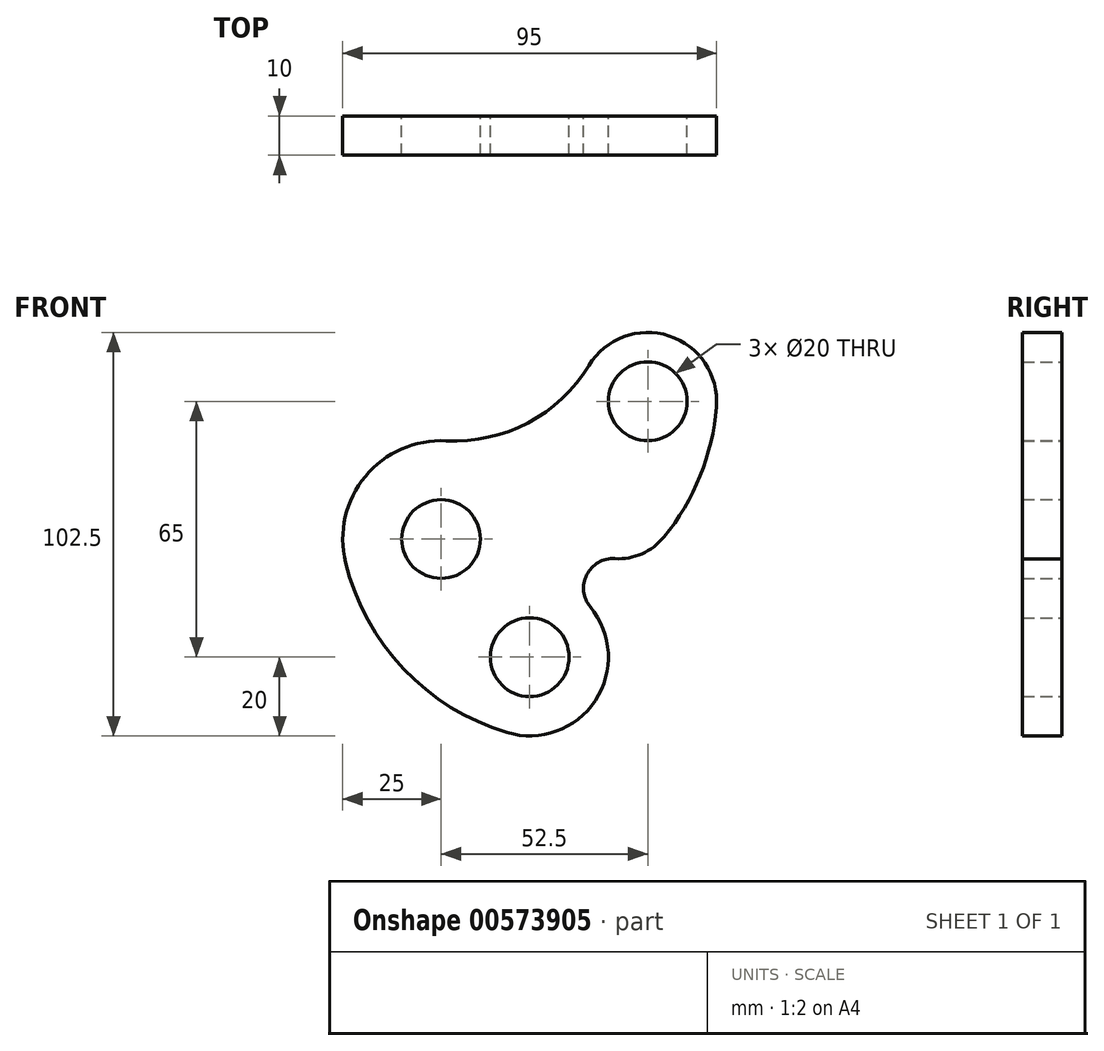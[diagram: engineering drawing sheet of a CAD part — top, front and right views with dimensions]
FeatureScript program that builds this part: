
annotation { "Feature Type Name" : "Feature", "Feature Type Description" : "" }
export const myFeature = defineFeature(function(context is Context, id is Id, definition is map)
    precondition{}
    {
        {
            var Q0;
            Q0=qCreatedBy(makeId("Front.planeOp"),FACE);
            var sketch = newSketch(context, id + "F0", { "sketchPlane" : qUnion([Q0])});
            skCircle(sketch, "E0", {"center": v(0, 0) * mm, "radius": 10 * mm});
            skCircle(sketch, "E1", {"center": v(22.5, -30) * mm, "radius": 10 * mm});
            skCircle(sketch, "E2", {"center": v(52.5, 35) * mm, "radius": 10 * mm});
            skArc(sketch, "E3", {"start": v(1.3, 24.97) * mm, "mid": v(-19.26, 15.94) * mm, "end": v(-24.28, -5.94) * mm});
            skArc(sketch, "E4", {"start": v(69.94, 33.58) * mm, "mid": v(57.9, 51.64) * mm, "end": v(37.55, 44.1) * mm});
            skArc(sketch, "E5", {"start": v(16.75, -49.16) * mm, "mid": v(39.17, -41.05) * mm, "end": v(37.9, -17.24) * mm});
            skArc(sketch, "E6", {"start": v(44.12, -4.97) * mm, "mid": v(51.03, -3.73) * mm, "end": v(56.62, 0.51) * mm});
            skArc(sketch, "E7", {"start": v(-24.28, -5.94) * mm, "mid": v(-9.51, -33) * mm, "end": v(16.75, -49.16) * mm});
            skArc(sketch, "E8", {"start": v(1.3, 24.97) * mm, "mid": v(22.07, 29.54) * mm, "end": v(37.55, 44.1) * mm});
            skArc(sketch, "E9", {"start": v(56.62, 0.51) * mm, "mid": v(65.8, 16.03) * mm, "end": v(69.94, 33.58) * mm});
            skArc(sketch, "E10", {"start": v(44.12, -4.97) * mm, "mid": v(37, -9.07) * mm, "end": v(37.9, -17.24) * mm});
            skSolve(sketch);
        }
        {
            var Q0;
            Q0 = qSketchRegion(id + "F0", true);
            extrude(context, id + "F1", {"entities" : qUnion([Q0]), "depth" : 10 * mm, "offsetDistance" : 25 * mm});
        }
    });
